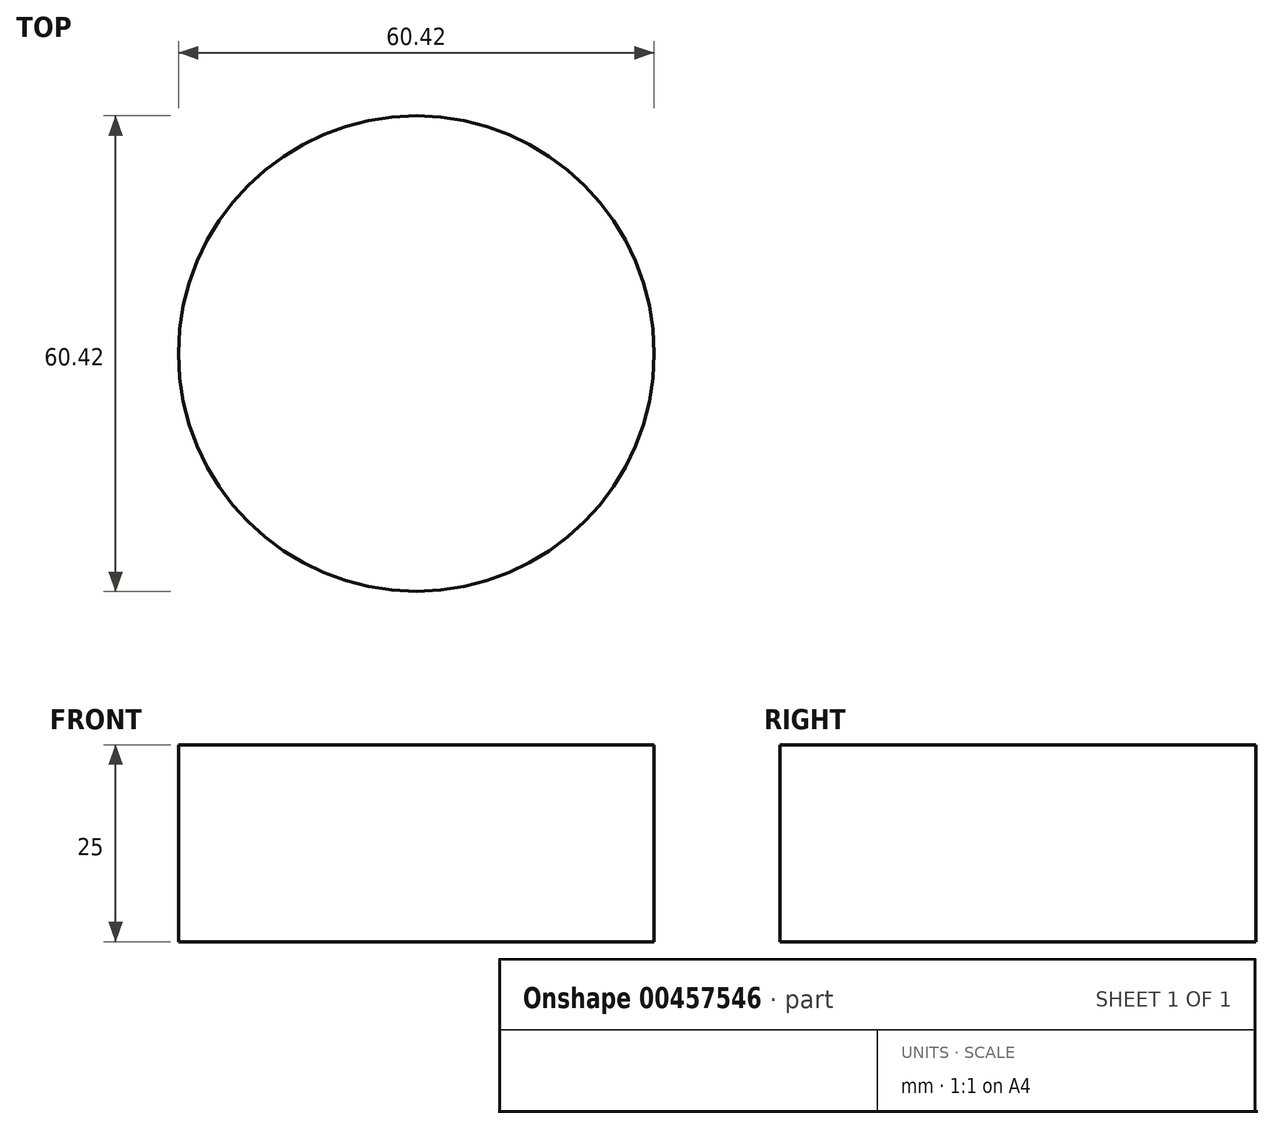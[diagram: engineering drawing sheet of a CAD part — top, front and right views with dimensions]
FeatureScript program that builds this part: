
annotation { "Feature Type Name" : "Feature", "Feature Type Description" : "" }
export const myFeature = defineFeature(function(context is Context, id is Id, definition is map)
    precondition{}
    {
        {
            var Q0;
            Q0=qCreatedBy(makeId("Top.planeOp"),FACE);
            var sketch = newSketch(context, id + "F0", { "sketchPlane" : qUnion([Q0])});
            skCircle(sketch, "E0", {"center": v(0, 0) * mm, "radius": 30.2 * mm});
            skSolve(sketch);
        }
        {
            var Q0;
            Q0=makeQuery(id+"F0.imprint","IMPRINT",FACE,{"disambiguationData":[TD([[makeQuery(id+"F0.imprint","IMPRINT",EDGE,{"derivedFrom":sQuery(id+"F0.wireOp",EDGE,"E0")}),1.0]])]});
            extrude(context, id + "F1", {"entities" : qUnion([Q0]), "depth" : 25 * mm});
        }
    });
